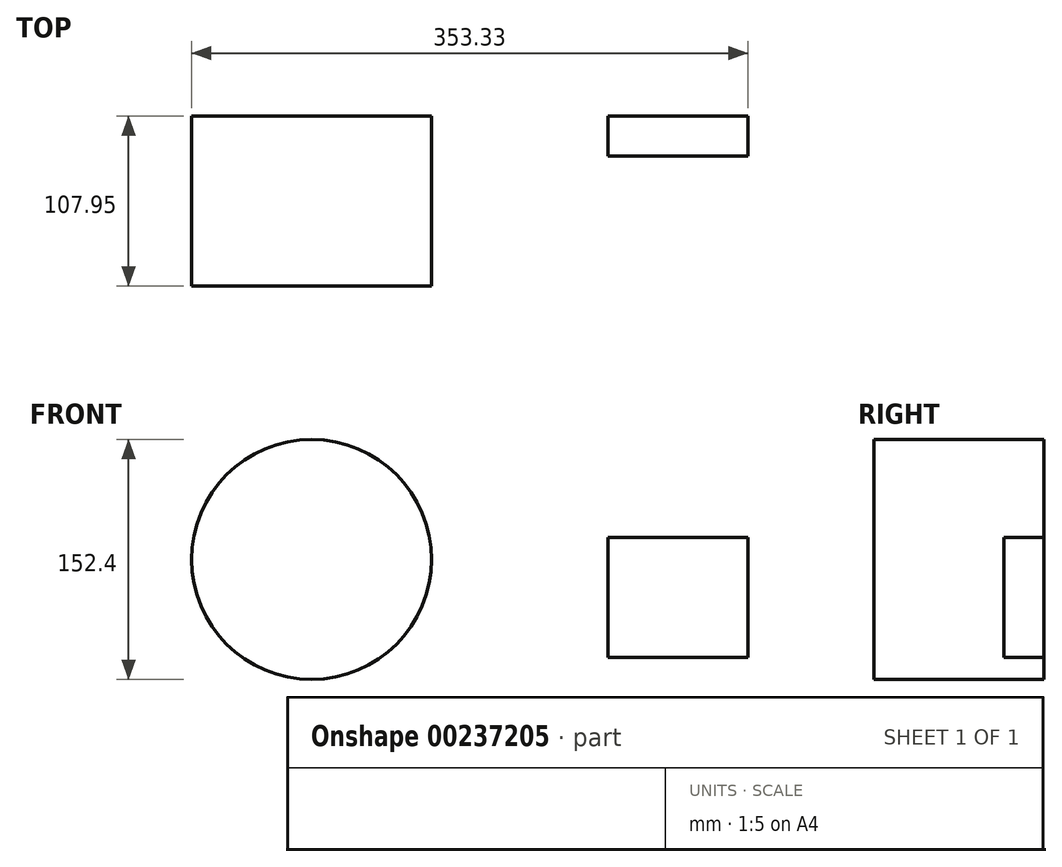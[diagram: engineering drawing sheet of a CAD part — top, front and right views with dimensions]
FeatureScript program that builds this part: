
annotation { "Feature Type Name" : "Feature", "Feature Type Description" : "" }
export const myFeature = defineFeature(function(context is Context, id is Id, definition is map)
    precondition{}
    {
        {
            var Q0;
            Q0=qCreatedBy(makeId("Front.planeOp"),FACE);
            var sketch = newSketch(context, id + "F0", { "sketchPlane" : qUnion([Q0])});
            skCircle(sketch, "E0", {"center": v(0, 0) * mm, "radius": 76.2 * mm});
            skSolve(sketch);
        }
        {
            var Q0;
            Q0=makeQuery(id+"F0.imprint","IMPRINT",FACE,{"disambiguationData":[TD([[makeQuery(id+"F0.imprint","IMPRINT",EDGE,{"derivedFrom":sQuery(id+"F0.wireOp",EDGE,"E0")}),1.0]])]});
            extrude(context, id + "F1", {"entities" : qUnion([Q0]), "depth" : 107.95 * mm});
        }
        {
            var Q0;
            Q0=qCreatedBy(makeId("Front.planeOp"),FACE);
            var sketch = newSketch(context, id + "F2", { "sketchPlane" : qUnion([Q0])});
            skLineSegment(sketch, "E1.bottom", {"start": v(188.23, 14.06) * mm, "end": v(277.13, 14.06) * mm});
            skLineSegment(sketch, "E1.top", {"start": v(188.23, -62.14) * mm, "end": v(277.13, -62.14) * mm});
            skLineSegment(sketch, "E1.left", {"start": v(188.23, 14.06) * mm, "end": v(188.23, -62.14) * mm});
            skLineSegment(sketch, "E1.right", {"start": v(277.13, 14.06) * mm, "end": v(277.13, -62.14) * mm});
            skSolve(sketch);
        }
        {
            var Q0;
            Q0=makeQuery(id+"F2.imprint","IMPRINT",FACE,{"disambiguationData":[TD([[makeQuery(id+"F2.imprint","IMPRINT",EDGE,{"derivedFrom":sQuery(id+"F2.wireOp",EDGE,"E1.bottom")}),-1.0]])]});
            extrude(context, id + "F3", {"entities" : qUnion([Q0]), "depth" : 25.4 * mm});
        }
    });
